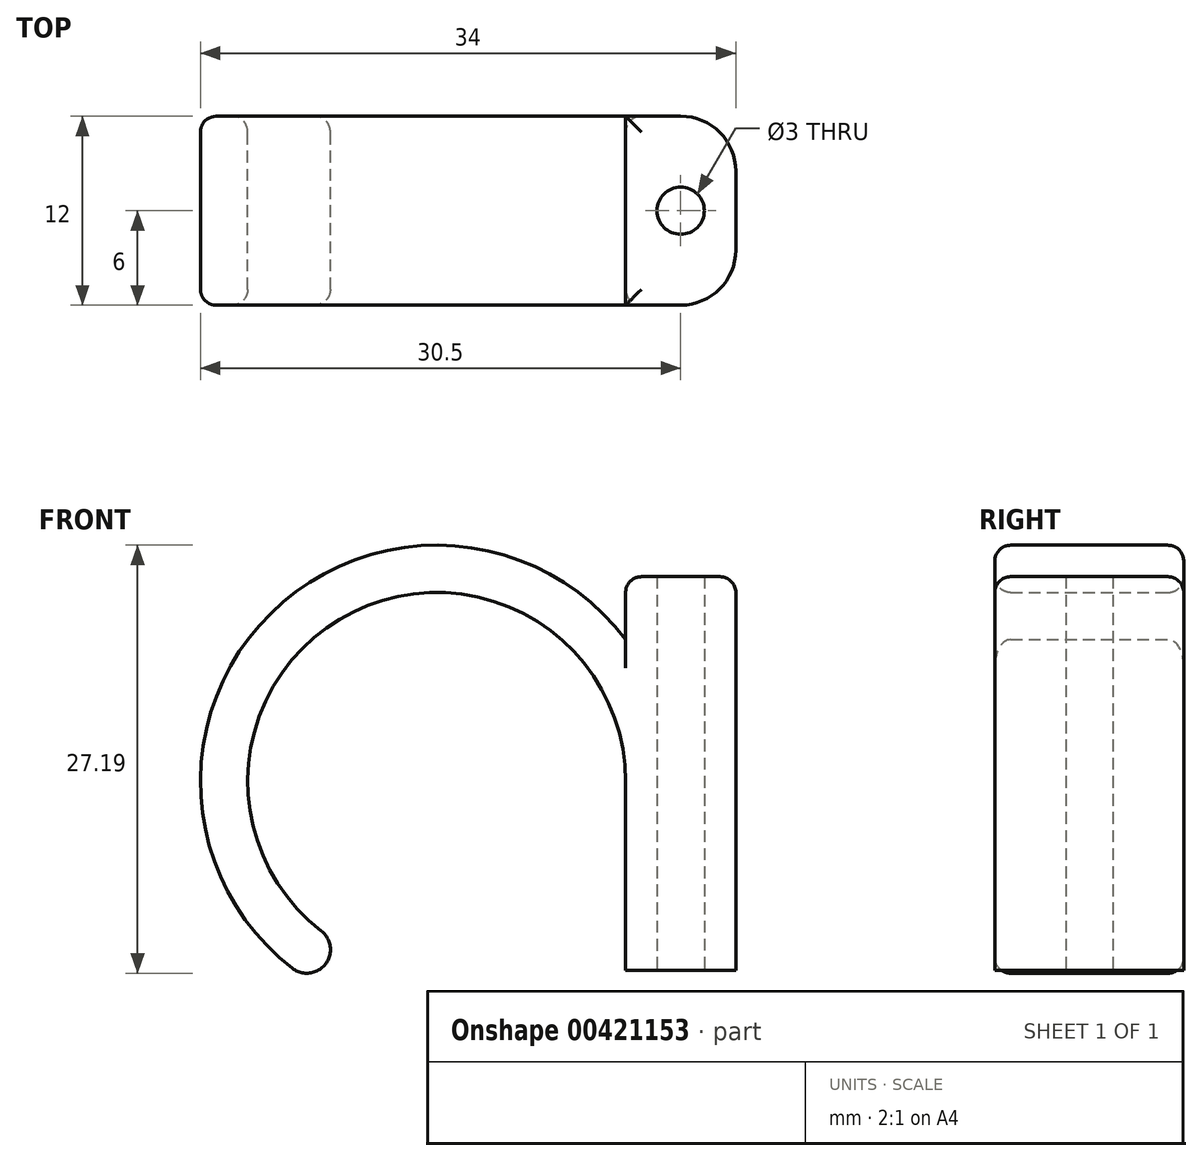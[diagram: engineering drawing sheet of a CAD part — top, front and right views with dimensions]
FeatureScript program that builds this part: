
annotation { "Feature Type Name" : "Feature", "Feature Type Description" : "" }
export const myFeature = defineFeature(function(context is Context, id is Id, definition is map)
    precondition{}
    {
        {
            var Q0;
            Q0=qCreatedBy(makeId("Front.planeOp"),FACE);
            var sketch = newSketch(context, id + "F0", { "sketchPlane" : qUnion([Q0])});
            skArc(sketch, "E0", {"start": v(12, 0) * mm, "mid": v(-5.3, 10.77) * mm, "end": v(-7.33, -9.5) * mm});
            skLineSegment(sketch, "E1.bottom", {"start": v(0, 0) * mm, "end": v(12, 0) * mm, "construction": true});
            skLineSegment(sketch, "E1.top", {"start": v(0, -12) * mm, "end": v(12, -12) * mm, "construction": true});
            skLineSegment(sketch, "E1.left", {"start": v(0, 0) * mm, "end": v(0, -12) * mm, "construction": true});
            skLineSegment(sketch, "E1.right", {"start": v(12, 0) * mm, "end": v(12, -12) * mm, "construction": true});
            skArc(sketch, "E2", {"start": v(12, 9) * mm, "mid": v(-10.53, 10.68) * mm, "end": v(-9.17, -11.87) * mm});
            skArc(sketch, "E3", {"start": v(-9.17, -11.87) * mm, "mid": v(-7.06, -11.6) * mm, "end": v(-7.33, -9.5) * mm});
            skLineSegment(sketch, "E4.bottom", {"start": v(12, -12) * mm, "end": v(19, -12) * mm});
            skLineSegment(sketch, "E4.top", {"start": v(12, 13) * mm, "end": v(19, 13) * mm});
            skLineSegment(sketch, "E4.left", {"start": v(12, -12) * mm, "end": v(12, 13) * mm});
            skLineSegment(sketch, "E4.right", {"start": v(19, -12) * mm, "end": v(19, 13) * mm});
            skSolve(sketch);
        }
        {
            var Q0;
            {var subQ0=sQuery(id+"F0.wireOp",EDGE,"E0");Q0=makeQuery(id+"F0.imprint","IMPRINT",FACE,{"disambiguationData":[TD([[makeQuery(id+"F0.imprint","IMPRINT",EDGE,{"derivedFrom":subQ0}),-1.0]])]});}
            var Q1;
            {var subQ3=sQuery(id+"F0.wireOp",EDGE,"E4.bottom");Q1=makeQuery(id+"F0.imprint","IMPRINT",FACE,{"disambiguationData":[TD([[makeQuery(id+"F0.imprint","IMPRINT",EDGE,{"derivedFrom":subQ3}),1.0]])]});}
            extrude(context, id + "F1", {"entities" : qUnion([Q0, Q1]), "depth" : 12 * mm});
        }
        {
            var Q0;
            Q0=makeQuery(id+"F1.opExtrude","CAP_EDGE",EDGE,{"disambiguationData":[OSD([sQuery(id+"F0.wireOp",EDGE,"E4.right")])],"isStart":false});
            var Q1;
            Q1=makeQuery(id+"F1.opExtrude","CAP_EDGE",EDGE,{"disambiguationData":[OSD([sQuery(id+"F0.wireOp",EDGE,"E4.right")])],"isStart":true});
            fillet(context, id + "F2", {"entities" : qUnion([Q0, Q1]), "radius" : 3.5 * mm, "tangentPropagation" : true, "allowEdgeOverflow" : false});
        }
        {
            var Q0;
            Q0=makeQuery(id+"F1.opExtrude","CAP_EDGE",EDGE,{"disambiguationData":[OSD([sQuery(id+"F0.wireOp",EDGE,"E0")])],"isStart":false});
            var Q1;
            Q1=makeQuery(id+"F1.opExtrude","CAP_EDGE",EDGE,{"disambiguationData":[OSD([sQuery(id+"F0.wireOp",EDGE,"E0")])],"isStart":true});
            var Q2;
            Q2=makeQuery(id+"F1.opExtrude","SWEPT_EDGE",EDGE,{"disambiguationData":[OSD([sQuery(id+"F0.wireOp",EDGE,"E4.top"),sQuery(id+"F0.wireOp",EDGE,"E4.left")])]});
            var Q3;
            Q3=makeQuery(id+"F2.opFillet","BLEND_EDGE",EDGE,{"blendedFrom":[makeQuery(id+"F1.opExtrude","CAP_EDGE",EDGE,{"disambiguationData":[OSD([sQuery(id+"F0.wireOp",EDGE,"E4.right")])],"isStart":false}),makeQuery(id+"F1.opExtrude","SWEPT_FACE",FACE,{"disambiguationData":[OSD([sQuery(id+"F0.wireOp",EDGE,"E4.top")])]})],"blendedInto":[makeQuery(id+"F1.opExtrude","SWEPT_FACE",FACE,{"disambiguationData":[OSD([sQuery(id+"F0.wireOp",EDGE,"E4.top")])]})]});
            fillet(context, id + "F3", {"entities" : qUnion([Q0, Q1, Q2, Q3]), "radius" : 1 * mm, "tangentPropagation" : true, "allowEdgeOverflow" : false});
        }
        {
            var Q0;
            Q0=makeQuery(id+"F1.opExtrude","SWEPT_FACE",FACE,{"disambiguationData":[OSD([sQuery(id+"F0.wireOp",EDGE,"E4.top")])]});
            var sketch = newSketch(context, id + "F4", { "sketchPlane" : qUnion([Q0])});
            skLineSegment(sketch, "E5", {"start": v(13, -6) * mm, "end": v(15.5, -6) * mm, "construction": true});
            skSolve(sketch);
        }
        {
            var Q0;
            Q0=sQuery(id+"F4.wireOp",VERTEX,"E5.end");
            var Q1;
            Q1=makeQuery(id+"F1.opExtrude","SWEPT_BODY",BODY,{"disambiguationData":[OSD([sQuery(id+"F0.wireOp",EDGE,"E0"),sQuery(id+"F0.wireOp",EDGE,"E2"),sQuery(id+"F0.wireOp",EDGE,"E3"),sQuery(id+"F0.wireOp",EDGE,"E4.bottom"),sQuery(id+"F0.wireOp",EDGE,"E4.top"),sQuery(id+"F0.wireOp",EDGE,"E4.left"),sQuery(id+"F0.wireOp",EDGE,"E4.right")])]});
            hole(context, id + "F5", {"style" : HoleStyle.SIMPLE, "endStyle" : HoleEndStyle.BLIND, "holeDiameter" : 3 * mm, "holeDepth" : 50 * mm, "isTappedThrough" : true, "tappedDepth" : 12 * mm, "tapClearance" : 3, "locations" : qUnion([Q0]), "scope" : qUnion([Q1])});
        }
    });
